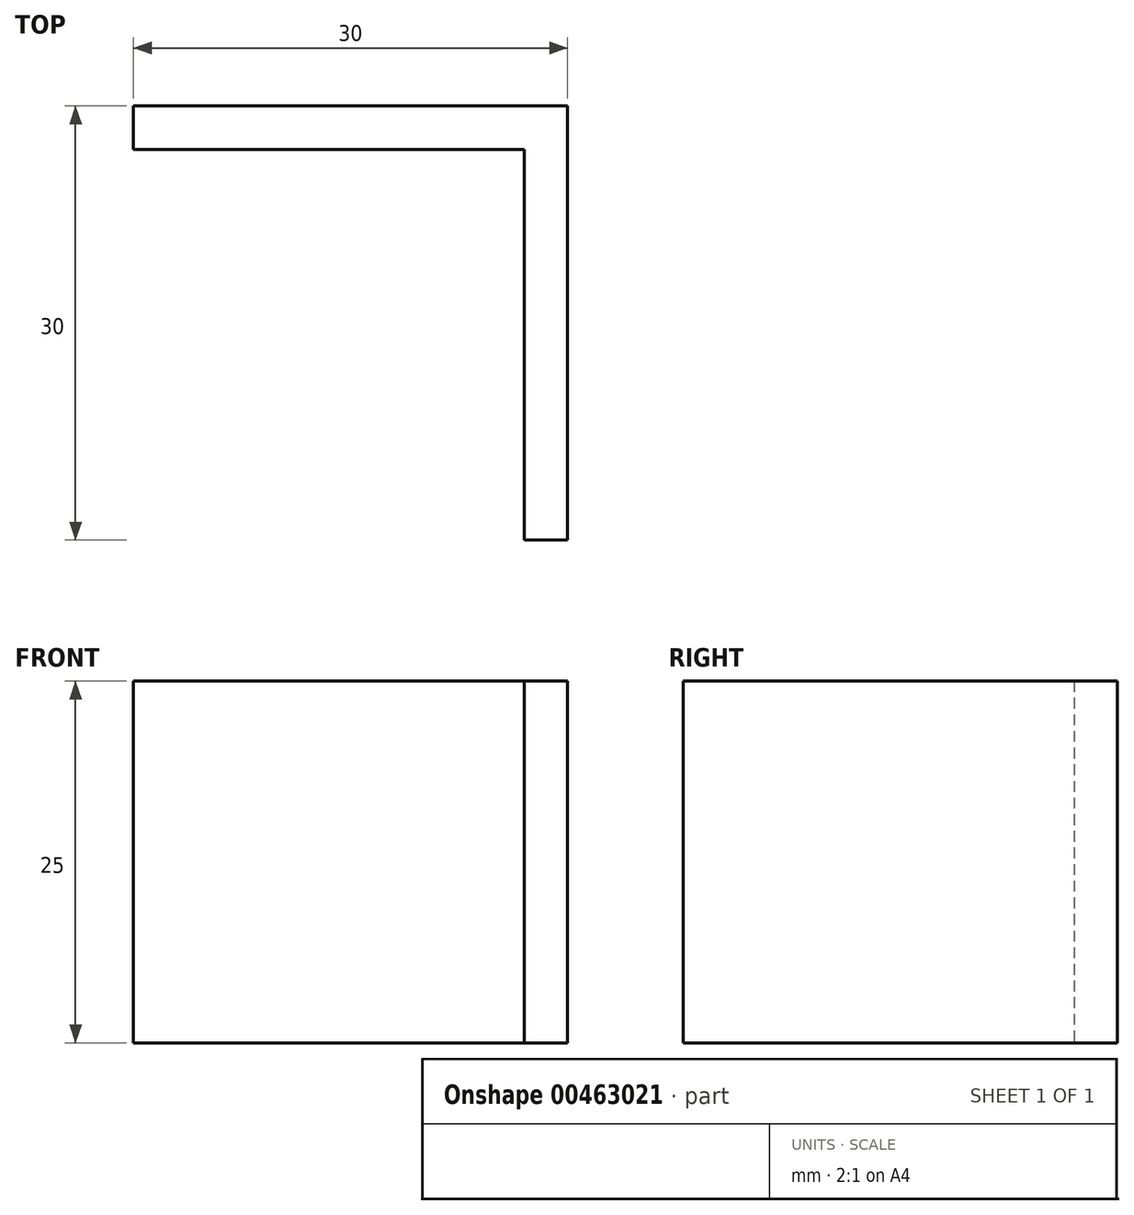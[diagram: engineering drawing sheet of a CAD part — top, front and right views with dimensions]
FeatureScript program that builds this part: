
annotation { "Feature Type Name" : "Feature", "Feature Type Description" : "" }
export const myFeature = defineFeature(function(context is Context, id is Id, definition is map)
    precondition{}
    {
        {
            var Q0;
            Q0=qCreatedBy(makeId("Top.planeOp"),FACE);
            var sketch = newSketch(context, id + "F0", { "sketchPlane" : qUnion([Q0])});
            skLineSegment(sketch, "E0", {"start": v(0, 0) * mm, "end": v(0, 30) * mm});
            skLineSegment(sketch, "E1", {"start": v(0, 30) * mm, "end": v(-30, 30) * mm});
            skLineSegment(sketch, "E2", {"start": v(-30, 30) * mm, "end": v(-30, 27) * mm});
            skLineSegment(sketch, "E3", {"start": v(-30, 27) * mm, "end": v(-3, 27) * mm});
            skLineSegment(sketch, "E4", {"start": v(-3, 27) * mm, "end": v(-3, 0) * mm});
            skLineSegment(sketch, "E5", {"start": v(-3, 0) * mm, "end": v(0, 0) * mm});
            skSolve(sketch);
        }
        {
            var Q0;
            Q0 = qSketchRegion(id + "F0", true);
            extrude(context, id + "F1", {"entities" : qUnion([Q0]), "depth" : 25 * mm});
        }
    });
